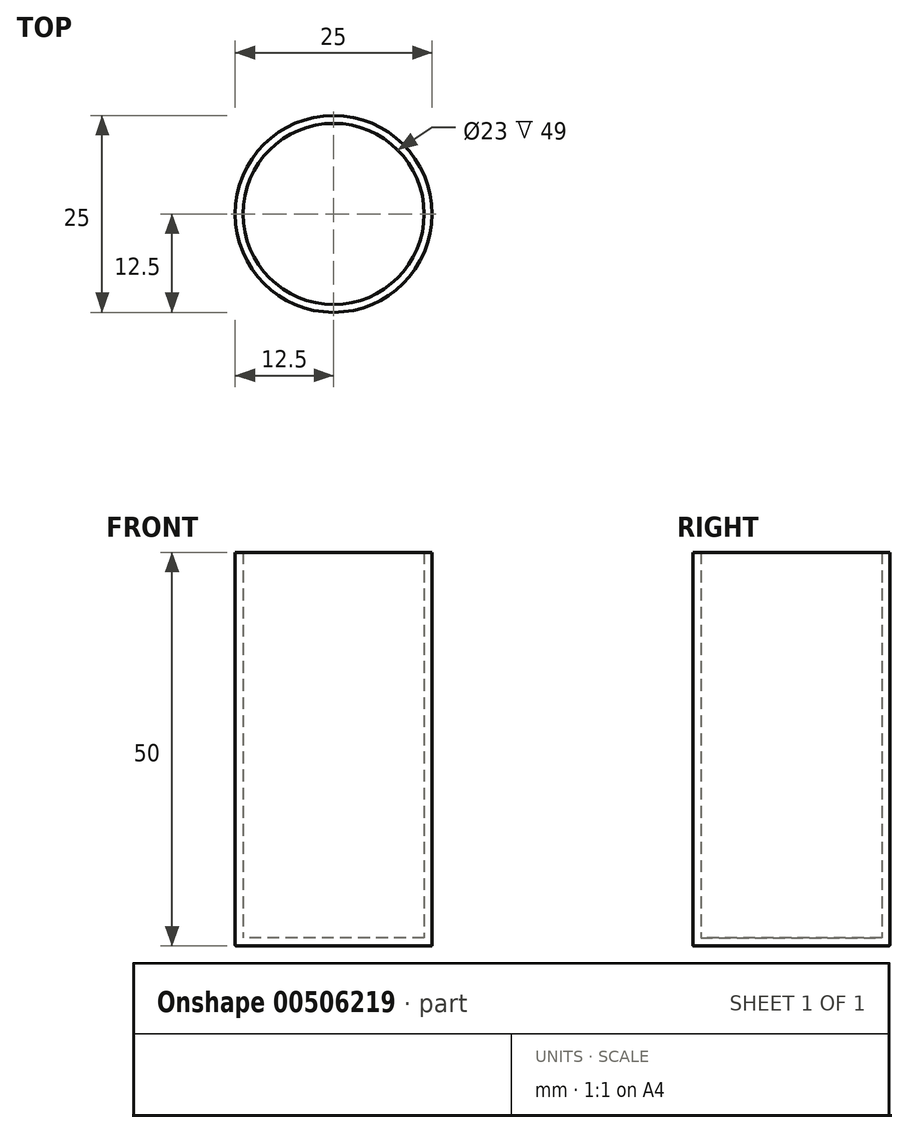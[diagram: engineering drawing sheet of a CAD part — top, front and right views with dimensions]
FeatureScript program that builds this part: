
annotation { "Feature Type Name" : "Feature", "Feature Type Description" : "" }
export const myFeature = defineFeature(function(context is Context, id is Id, definition is map)
    precondition{}
    {
        {
            var Q0;
            Q0=qCreatedBy(makeId("Top.planeOp"),FACE);
            var sketch = newSketch(context, id + "F0", { "sketchPlane" : qUnion([Q0])});
            skCircle(sketch, "E0", {"center": v(0, 0) * mm, "radius": 12.5 * mm});
            skSolve(sketch);
        }
        {
            var Q0;
            Q0=makeQuery(id+"F0.imprint","IMPRINT",FACE,{"disambiguationData":[TD([[makeQuery(id+"F0.imprint","IMPRINT",EDGE,{"derivedFrom":sQuery(id+"F0.wireOp",EDGE,"E0")}),1.0]])]});
            extrude(context, id + "F1", {"entities" : qUnion([Q0]), "depth" : 50 * mm});
        }
        {
            var Q0;
            Q0=makeQuery(id+"F1.opExtrude","CAP_FACE",FACE,{"disambiguationData":[OSD([sQuery(id+"F0.wireOp",EDGE,"E0")])],"isStart":false});
            shell(context, id + "F2", {"entities" : qUnion([Q0]), "thickness" : 1 * mm});
        }
        {
            var Q0;
            Q0=makeQuery(id+"F1.opExtrude","CAP_EDGE",EDGE,{"disambiguationData":[OSD([sQuery(id+"F0.wireOp",EDGE,"E0")])],"isStart":true});
            fillet(context, id + "F3", {"entities" : qUnion([Q0]), "radius" : 0.1 * mm, "tangentPropagation" : true, "allowEdgeOverflow" : false});
        }
    });
